# Revit family: Стол письменный корпусный без тумбы Юнитекс ПФ
name_source: partatom
category: Оборудование
revit_build: Autodesk Revit 2017 (Build: 20170118_1100(x64)
units: mm (PartAtom-declared; Revit-internal decimal feet)

## family parameters
Всегда вертикально = Да
На основе рабочей плоскости = Нет
Общий = Нет
При загрузке вырезать с полостями = Нет
Размер круглого соединителя = Использовать диаметр
Тип детали = Нормальный
Точка расчета площади = Нет

## types (6) — shared parameters
Общ_Высота = 750 мм
Общ_Единицы измерения = шт.
Общ_Наименование = Стол рабочий, корпусный, без тумбы
Общ_Поставщик = Юнитекс

## per-type parameters (varying)
| type | Группа модели | Изготовитель | Общ_Глубина | Общ_Тип, марка | Общ_Ширина |
| 1400х600х750 | ТХ | Severin | 600 мм | ПФ 0162 | 1400 мм |
| 1400х800х750 | ТХ | Ant | 800 мм | ПФ 102 | 1400 мм |
| 1200х600х750 | ТХ | Ant | 600 мм | ПФ 0161 | 1200 мм |
| 1200х800х750 | ТХ | Ant | 800 мм | ПФ 101 | 1200 мм |
| 1600х800х750 | ТХ | Ant | 800 мм | ПФ 103 | 1600 мм |
| 1600х600х750 |  | Severin | 600 мм | ПФ 0163 | 1600 мм |
